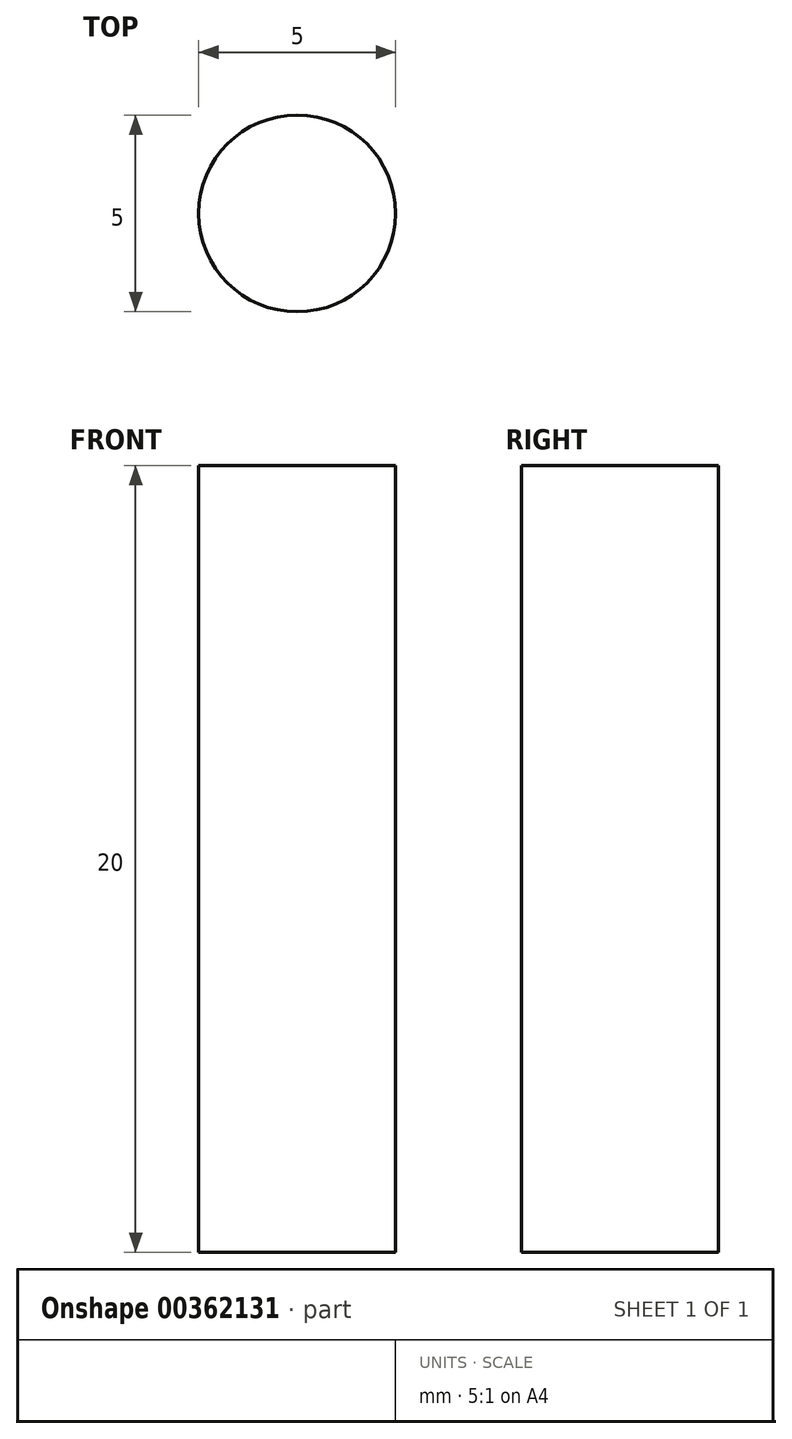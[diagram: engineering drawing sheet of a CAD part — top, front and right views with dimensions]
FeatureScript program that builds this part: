
annotation { "Feature Type Name" : "Feature", "Feature Type Description" : "" }
export const myFeature = defineFeature(function(context is Context, id is Id, definition is map)
    precondition{}
    {
        {
            var Q0;
            Q0=qCreatedBy(makeId("Top.planeOp"),FACE);
            var sketch = newSketch(context, id + "F0", { "sketchPlane" : qUnion([Q0])});
            skCircle(sketch, "E0", {"center": v(0, 0) * mm, "radius": 2.5 * mm});
            skSolve(sketch);
        }
        {
            var Q0;
            Q0=makeQuery(id+"F0.imprint","IMPRINT",FACE,{"disambiguationData":[TD([[makeQuery(id+"F0.imprint","IMPRINT",EDGE,{"derivedFrom":sQuery(id+"F0.wireOp",EDGE,"E0")}),1.0]])]});
            extrude(context, id + "F1", {"entities" : qUnion([Q0]), "depth" : 20 * mm});
        }
    });
